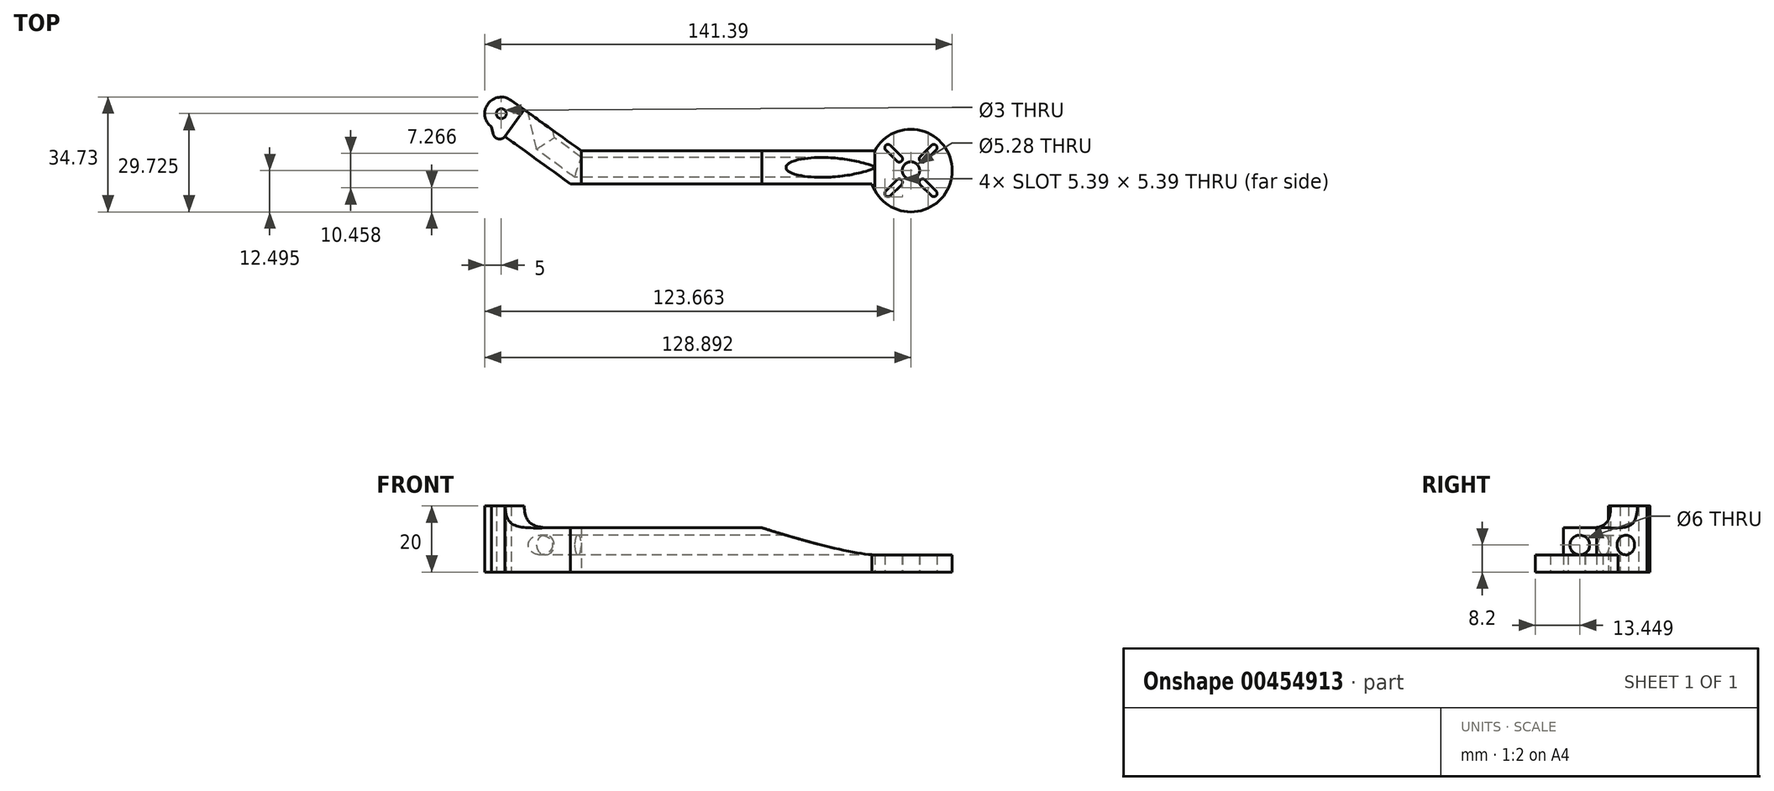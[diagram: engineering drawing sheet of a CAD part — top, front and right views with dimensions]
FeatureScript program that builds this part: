
annotation { "Feature Type Name" : "Feature", "Feature Type Description" : "" }
export const myFeature = defineFeature(function(context is Context, id is Id, definition is map)
    precondition{}
    {
        {
            var Q0;
            Q0=qCreatedBy(makeId("Top.planeOp"),FACE);
            var sketch = newSketch(context, id + "F0", { "sketchPlane" : qUnion([Q0])});
            skLineSegment(sketch, "E0", {"start": v(-161.05, 41.93) * mm, "end": v(-137.16, 59.15) * mm, "construction": true});
            skLineSegment(sketch, "E1", {"start": v(-137.16, 59.15) * mm, "end": v(-37.16, 59.15) * mm, "construction": true});
            skArc(sketch, "E2", {"start": v(-48.13, 53.17) * mm, "mid": v(-24.7, 60.23) * mm, "end": v(-49, 63.17) * mm});
            skLineSegment(sketch, "E3.0", {"start": v(-158.07, 37.9) * mm, "end": v(-136.9, 53.17) * mm});
            skLineSegment(sketch, "E4.0", {"start": v(-164.03, 45.94) * mm, "end": v(-140.14, 63.17) * mm});
            skArc(sketch, "E5", {"start": v(-164.03, 45.94) * mm, "mid": v(-165.07, 38.95) * mm, "end": v(-158.07, 37.9) * mm});
            skLineSegment(sketch, "E6", {"start": v(-140.14, 63.17) * mm, "end": v(-49, 63.17) * mm});
            skLineSegment(sketch, "E7", {"start": v(-136.9, 53.17) * mm, "end": v(-48.13, 53.17) * mm});
            skCircle(sketch, "E8", {"center": v(-37.16, 59.15) * mm, "radius": 2.64 * mm});
            skArc(sketch, "E9.0.startCap", {"start": v(-44.79, 65.37) * mm, "mid": v(-44.79, 66.78) * mm, "end": v(-43.37, 66.78) * mm});
            skArc(sketch, "E9.0.endCap", {"start": v(-39.99, 63.4) * mm, "mid": v(-39.99, 61.98) * mm, "end": v(-41.4, 61.98) * mm});
            skLineSegment(sketch, "E9.0.left", {"start": v(-43.37, 66.78) * mm, "end": v(-39.99, 63.4) * mm});
            skLineSegment(sketch, "E9.0.right", {"start": v(-44.79, 65.37) * mm, "end": v(-41.4, 61.98) * mm});
            skLineSegment(sketch, "E10", {"start": v(-37.16, 59.15) * mm, "end": v(-37.16, 66.76) * mm, "construction": true});
            skArc(sketch, "E11.MirrorCS", {"start": v(-29.53, 65.37) * mm, "mid": v(-29.53, 66.78) * mm, "end": v(-30.94, 66.78) * mm});
            skArc(sketch, "E12.MirrorCS", {"start": v(-34.33, 63.4) * mm, "mid": v(-34.33, 61.98) * mm, "end": v(-32.92, 61.98) * mm});
            skLineSegment(sketch, "E13.MirrorCS", {"start": v(-29.53, 65.37) * mm, "end": v(-32.92, 61.98) * mm});
            skLineSegment(sketch, "E14.MirrorCS", {"start": v(-30.94, 66.78) * mm, "end": v(-34.33, 63.4) * mm});
            skLineSegment(sketch, "E15.MirrorCS", {"start": v(-30.94, 51.52) * mm, "end": v(-34.33, 54.91) * mm});
            skArc(sketch, "E16.MirrorCS", {"start": v(-29.53, 52.94) * mm, "mid": v(-29.53, 51.52) * mm, "end": v(-30.94, 51.52) * mm});
            skLineSegment(sketch, "E17.MirrorCS", {"start": v(-29.53, 52.94) * mm, "end": v(-32.92, 56.33) * mm});
            skArc(sketch, "E18.MirrorCS", {"start": v(-34.33, 54.91) * mm, "mid": v(-34.33, 56.33) * mm, "end": v(-32.92, 56.33) * mm});
            skLineSegment(sketch, "E19.MirrorCS", {"start": v(-44.79, 52.94) * mm, "end": v(-41.4, 56.33) * mm});
            skLineSegment(sketch, "E20.MirrorCS", {"start": v(-43.37, 51.52) * mm, "end": v(-39.99, 54.91) * mm});
            skArc(sketch, "E21.MirrorCS", {"start": v(-39.99, 54.91) * mm, "mid": v(-39.99, 56.33) * mm, "end": v(-41.4, 56.33) * mm});
            skArc(sketch, "E22.MirrorCS", {"start": v(-44.79, 52.94) * mm, "mid": v(-44.79, 51.52) * mm, "end": v(-43.37, 51.52) * mm});
            skCircle(sketch, "E23", {"center": v(-161.05, 41.93) * mm, "radius": 1.5 * mm});
            skLineSegment(sketch, "E24", {"start": v(-37.16, 59.15) * mm, "end": v(-44.76, 66.76) * mm, "construction": true});
            skSolve(sketch);
        }
        {
            var Q0;
            Q0=qSketchRegion(id+"F0",true);
            extrude(context, id + "F1", {"entities" : qUnion([Q0]), "depth" : 20 * mm});
        }
        {
            var Q0;
            Q0=makeQuery(id+"F1.opExtrude","SWEPT_FACE",FACE,{"disambiguationData":[OSD([sQuery(id+"F0.wireOp",EDGE,"E7")])]});
            var sketch = newSketch(context, id + "F2", { "sketchPlane" : qUnion([Q0])});
            skFitSpline(sketch, "E25", {"points": [v(-48.13, 5.2) * mm, v(-101.02, 20) * mm], "startDerivative": vector(-37.65, 1.6) * mm, "endDerivative": vector(-23.18, 9.57) * mm});
            skLineSegment(sketch, "E26", {"start": v(-48.13, 5.2) * mm, "end": v(-22.68, 5.2) * mm});
            skLineSegment(sketch, "E27", {"start": v(-22.68, 5.2) * mm, "end": v(-24.44, 23.02) * mm});
            skLineSegment(sketch, "E28", {"start": v(-24.44, 23.02) * mm, "end": v(-102.95, 23.97) * mm});
            skLineSegment(sketch, "E29", {"start": v(-102.95, 23.97) * mm, "end": v(-109.86, 20) * mm});
            skLineSegment(sketch, "E30", {"start": v(-82.25, 13.43) * mm, "end": v(-136.9, 13.43) * mm});
            skLineSegment(sketch, "E31", {"start": v(-136.9, 13.43) * mm, "end": v(-136.9, 24.34) * mm});
            skLineSegment(sketch, "E32", {"start": v(-136.9, 24.34) * mm, "end": v(-109.86, 20) * mm});
            skSolve(sketch);
        }
        {
            var Q0;
            Q0=qSketchRegion(id+"F2",true);
            extrude(context, id + "F3", {"entities" : qUnion([Q0]), "operationType" : NewBodyOperationType.REMOVE, "oppositeDirection" : true, "depth" : 25 * mm, "hasSecondDirection" : true, "secondDirectionOppositeDirection" : false, "secondDirectionDepth" : 25 * mm});
        }
        {
            var Q0;
            Q0=makeQuery(id+"F1.opExtrude","SWEPT_FACE",FACE,{"disambiguationData":[OSD([sQuery(id+"F0.wireOp",EDGE,"E4.0")])]});
            var sketch = newSketch(context, id + "F4", { "sketchPlane" : qUnion([Q0])});
            skPoint(sketch, "E33.0", {"position": v(74.1, 13.43) * mm});
            skLineSegment(sketch, "E34.0", {"start": v(106.17, 20) * mm, "end": v(76.72, 20) * mm, "construction": true});
            skFitSpline(sketch, "E35", {"points": [v(74.1, 13.43) * mm, v(101.18, 20) * mm], "startDerivative": vector(56.52, 1.22) * mm, "endDerivative": vector(1.22, 26.42) * mm});
            skLineSegment(sketch, "E36", {"start": v(74.1, 13.43) * mm, "end": v(73.63, 25.15) * mm});
            skLineSegment(sketch, "E37", {"start": v(73.63, 25.15) * mm, "end": v(97.88, 26.12) * mm});
            skLineSegment(sketch, "E38", {"start": v(97.88, 26.12) * mm, "end": v(101.18, 20) * mm});
            skSolve(sketch);
        }
        {
            var Q0;
            Q0=qSketchRegion(id+"F4",true);
            extrude(context, id + "F5", {"entities" : qUnion([Q0]), "operationType" : NewBodyOperationType.REMOVE, "oppositeDirection" : true, "depth" : 25 * mm});
        }
        {
            var Q0;
            Q0=makeQuery(id+"F3.boolean.opBoolean","COPY",FACE,{"derivedFrom":makeQuery(id+"F3.opExtrude","SWEPT_FACE",FACE,{"disambiguationData":[OSD([sQuery(id+"F2.wireOp",EDGE,"E26")])]})});
            var sketch = newSketch(context, id + "F6", { "sketchPlane" : qUnion([Q0])});
            skLineSegment(sketch, "E39", {"start": v(-86.71, 58.17) * mm, "end": v(-61.2, 58.17) * mm});
            skLineSegment(sketch, "E40", {"start": v(-86.71, 58.17) * mm, "end": v(-137.85, 58.17) * mm});
            skLineSegment(sketch, "E41", {"start": v(-147.68, 50.92) * mm, "end": v(-156.98, 10.35) * mm});
            skLineSegment(sketch, "E42.trimOffspring", {"start": v(-147.68, 50.92) * mm, "end": v(-137.85, 58.17) * mm});
            skSolve(sketch);
        }
        {
            var Q0;
            Q0=makeQuery(id+"F3.boolean.opBoolean","COPY",EDGE,{"derivedFrom":makeQuery(id+"F3.opExtrude","SWEPT_EDGE",EDGE,{"disambiguationData":[OSD([sQuery(id+"F0.wireOp",EDGE,"E2"),sQuery(id+"F0.wireOp",EDGE,"E7"),sQuery(id+"F2.wireOp",EDGE,"E25"),sQuery(id+"F2.wireOp",EDGE,"E26")])]})});
            cPlane(context, id + "F7", {"entities" : qUnion([Q0]), "cplaneType" : CPlaneType.LINE_ANGLE, "offset" : 25 * mm, "angle" : 90 * degree, "width" : 150 * mm, "height" : 150 * mm});
        }
        {
            var Q0;
            Q0=qCreatedBy(id+"F7.planeOp",FACE);
            var sketch = newSketch(context, id + "F8", { "sketchPlane" : qUnion([Q0])});
            skLineSegment(sketch, "E43.0", {"start": v(65.14, 5.2) * mm, "end": v(53.17, 5.2) * mm, "construction": true});
            skCircle(sketch, "E44", {"center": v(58.2, 8.2) * mm, "radius": 3 * mm});
            skSolve(sketch);
        }
        {
            var Q0;
            Q0=qSketchRegion(id+"F8",true);
            var Q1;
            Q1=qConstructionFilter(qBodyType(qCreatedBy(id+"F6",EDGE),BodyType.WIRE),ConstructionObject.NO);
            sweep(context, id + "F9", {"operationType" : NewBodyOperationType.REMOVE, "profiles" : qUnion([Q0]), "path" : qUnion([Q1])});
        }
        {
            var Q0;
            Q0=makeQuery(id+"F1.opExtrude","CAP_FACE",FACE,{"disambiguationData":[OSD([sQuery(id+"F0.wireOp",EDGE,"E2"),sQuery(id+"F0.wireOp",EDGE,"E3.0"),sQuery(id+"F0.wireOp",EDGE,"E4.0"),sQuery(id+"F0.wireOp",EDGE,"E5"),sQuery(id+"F0.wireOp",EDGE,"E6"),sQuery(id+"F0.wireOp",EDGE,"E7"),sQuery(id+"F0.wireOp",EDGE,"E8"),sQuery(id+"F0.wireOp",EDGE,"E9.0.startCap"),sQuery(id+"F0.wireOp",EDGE,"E9.0.endCap"),sQuery(id+"F0.wireOp",EDGE,"E9.0.left"),sQuery(id+"F0.wireOp",EDGE,"E9.0.right"),sQuery(id+"F0.wireOp",EDGE,"E11.MirrorCS"),sQuery(id+"F0.wireOp",EDGE,"E12.MirrorCS"),sQuery(id+"F0.wireOp",EDGE,"E13.MirrorCS"),sQuery(id+"F0.wireOp",EDGE,"E14.MirrorCS"),sQuery(id+"F0.wireOp",EDGE,"E15.MirrorCS"),sQuery(id+"F0.wireOp",EDGE,"E16.MirrorCS"),sQuery(id+"F0.wireOp",EDGE,"E17.MirrorCS"),sQuery(id+"F0.wireOp",EDGE,"E18.MirrorCS"),sQuery(id+"F0.wireOp",EDGE,"E19.MirrorCS"),sQuery(id+"F0.wireOp",EDGE,"E20.MirrorCS"),sQuery(id+"F0.wireOp",EDGE,"E21.MirrorCS"),sQuery(id+"F0.wireOp",EDGE,"E22.MirrorCS"),sQuery(id+"F0.wireOp",EDGE,"E23")])],"isStart":true});
            var sketch = newSketch(context, id + "F10", { "sketchPlane" : qUnion([Q0])});
            skLineSegment(sketch, "E45", {"start": v(-164.03, -45.94) * mm, "end": v(-159.98, -48.86) * mm});
            skLineSegment(sketch, "E46", {"start": v(-159.98, -48.86) * mm, "end": v(-162.43, -52.25) * mm});
            skLineSegment(sketch, "E47", {"start": v(-162.43, -52.25) * mm, "end": v(-164.03, -45.94) * mm});
            skPoint(sketch, "E48.0", {"position": v(-159.98, -48.86) * mm});
            skSolve(sketch);
        }
        {
            var Q0;
            Q0=makeQuery(id+"F10.imprint","IMPRINT",FACE,{"disambiguationData":[TD([[makeQuery(id+"F10.imprint","IMPRINT",EDGE,{"derivedFrom":sQuery(id+"F10.wireOp",EDGE,"E45")}),-1.0]])]});
            extrude(context, id + "F11", {"entities" : qUnion([Q0]), "operationType" : NewBodyOperationType.ADD, "oppositeDirection" : true, "depth" : 20 * mm});
        }
        {
            var Q0;
            Q0=makeQuery(id+"F11.opExtrude","SWEPT_EDGE",EDGE,{"disambiguationData":[OSD([sQuery(id+"F10.wireOp",EDGE,"E46"),sQuery(id+"F10.wireOp",EDGE,"E47")])]});
            fillet(context, id + "F12", {"entities" : qUnion([Q0]), "radius" : 2 * mm, "tangentPropagation" : true, "allowEdgeOverflow" : false});
        }
        {
            var Q0;
            Q0=makeQuery(id+"F1.opExtrude","SWEPT_BODY",BODY,{"disambiguationData":[OSD([sQuery(id+"F0.wireOp",EDGE,"E2"),sQuery(id+"F0.wireOp",EDGE,"E3.0"),sQuery(id+"F0.wireOp",EDGE,"E4.0"),sQuery(id+"F0.wireOp",EDGE,"E5"),sQuery(id+"F0.wireOp",EDGE,"E6"),sQuery(id+"F0.wireOp",EDGE,"E7"),sQuery(id+"F0.wireOp",EDGE,"E8"),sQuery(id+"F0.wireOp",EDGE,"E9.0.startCap"),sQuery(id+"F0.wireOp",EDGE,"E9.0.endCap"),sQuery(id+"F0.wireOp",EDGE,"E9.0.left"),sQuery(id+"F0.wireOp",EDGE,"E9.0.right"),sQuery(id+"F0.wireOp",EDGE,"E11.MirrorCS"),sQuery(id+"F0.wireOp",EDGE,"E12.MirrorCS"),sQuery(id+"F0.wireOp",EDGE,"E13.MirrorCS"),sQuery(id+"F0.wireOp",EDGE,"E14.MirrorCS"),sQuery(id+"F0.wireOp",EDGE,"E15.MirrorCS"),sQuery(id+"F0.wireOp",EDGE,"E16.MirrorCS"),sQuery(id+"F0.wireOp",EDGE,"E17.MirrorCS"),sQuery(id+"F0.wireOp",EDGE,"E18.MirrorCS"),sQuery(id+"F0.wireOp",EDGE,"E19.MirrorCS"),sQuery(id+"F0.wireOp",EDGE,"E20.MirrorCS"),sQuery(id+"F0.wireOp",EDGE,"E21.MirrorCS"),sQuery(id+"F0.wireOp",EDGE,"E22.MirrorCS"),sQuery(id+"F0.wireOp",EDGE,"E23")])]});
            var Q1;
            Q1=qCreatedBy(makeId("Front.planeOp"),FACE);
            mirror(context, id + "F13", {"entities" : qUnion([Q0]), "mirrorPlane" : qUnion([Q1])});
        }
        {
            var Q0;
            Q0=makeQuery(id+"F11.boolean.opBoolean","MERGE",FACE,{"derivedFrom":[makeQuery(id+"F1.opExtrude","CAP_FACE",FACE,{"disambiguationData":[OSD([sQuery(id+"F0.wireOp",EDGE,"E2"),sQuery(id+"F0.wireOp",EDGE,"E3.0"),sQuery(id+"F0.wireOp",EDGE,"E4.0"),sQuery(id+"F0.wireOp",EDGE,"E5"),sQuery(id+"F0.wireOp",EDGE,"E6"),sQuery(id+"F0.wireOp",EDGE,"E7"),sQuery(id+"F0.wireOp",EDGE,"E8"),sQuery(id+"F0.wireOp",EDGE,"E9.0.startCap"),sQuery(id+"F0.wireOp",EDGE,"E9.0.endCap"),sQuery(id+"F0.wireOp",EDGE,"E9.0.left"),sQuery(id+"F0.wireOp",EDGE,"E9.0.right"),sQuery(id+"F0.wireOp",EDGE,"E11.MirrorCS"),sQuery(id+"F0.wireOp",EDGE,"E12.MirrorCS"),sQuery(id+"F0.wireOp",EDGE,"E13.MirrorCS"),sQuery(id+"F0.wireOp",EDGE,"E14.MirrorCS"),sQuery(id+"F0.wireOp",EDGE,"E15.MirrorCS"),sQuery(id+"F0.wireOp",EDGE,"E16.MirrorCS"),sQuery(id+"F0.wireOp",EDGE,"E17.MirrorCS"),sQuery(id+"F0.wireOp",EDGE,"E18.MirrorCS"),sQuery(id+"F0.wireOp",EDGE,"E19.MirrorCS"),sQuery(id+"F0.wireOp",EDGE,"E20.MirrorCS"),sQuery(id+"F0.wireOp",EDGE,"E21.MirrorCS"),sQuery(id+"F0.wireOp",EDGE,"E22.MirrorCS"),sQuery(id+"F0.wireOp",EDGE,"E23")])],"isStart":false}),makeQuery(id+"F11.opExtrude","CAP_FACE",FACE,{"disambiguationData":[OSD([sQuery(id+"F10.wireOp",EDGE,"E45"),sQuery(id+"F10.wireOp",EDGE,"E46"),sQuery(id+"F10.wireOp",EDGE,"E47")])],"isStart":false})]});
            var sketch = newSketch(context, id + "F14", { "sketchPlane" : qUnion([Q0])});
            skLineSegment(sketch, "E49.bottom", {"start": v(-193.14, 0) * mm, "end": v(-10.6, 0) * mm});
            skLineSegment(sketch, "E49.top", {"start": v(-193.14, 147.07) * mm, "end": v(-10.6, 147.07) * mm});
            skLineSegment(sketch, "E49.left", {"start": v(-193.14, 0) * mm, "end": v(-193.14, 147.07) * mm});
            skLineSegment(sketch, "E49.right", {"start": v(-10.6, 0) * mm, "end": v(-10.6, 147.07) * mm});
            skSolve(sketch);
        }
        {
            var Q0;
            Q0 = qSketchRegion(id + "F14", true);
            extrude(context, id + "F15", {"entities" : qUnion([Q0]), "operationType" : NewBodyOperationType.REMOVE, "oppositeDirection" : true, "depth" : 27 * mm});
        }
    });
